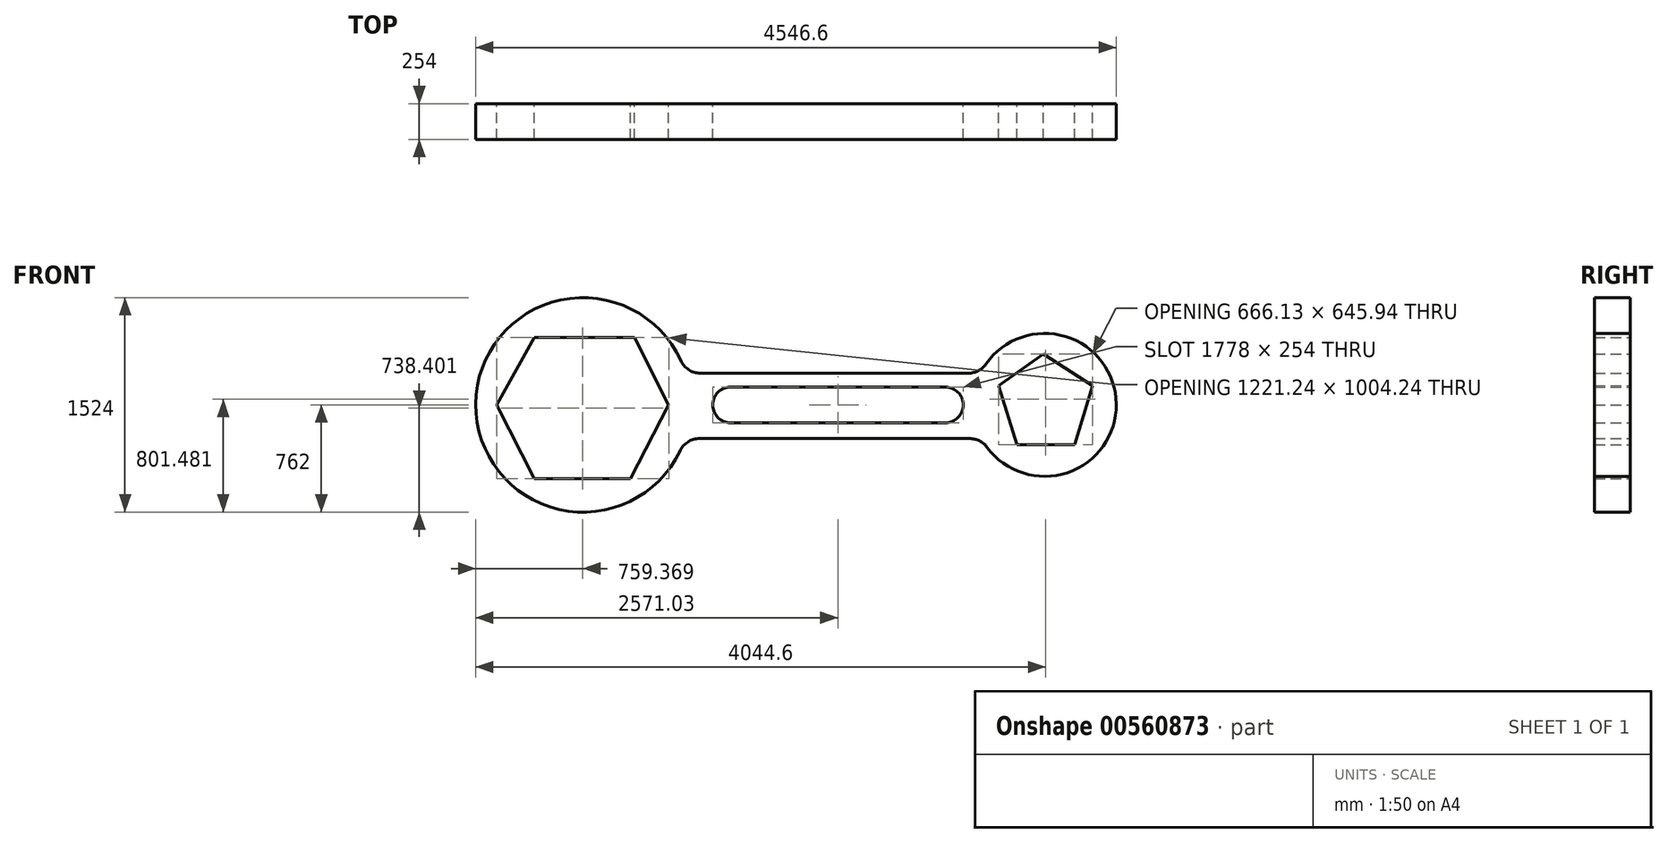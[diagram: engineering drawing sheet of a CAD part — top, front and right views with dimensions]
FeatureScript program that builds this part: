
annotation { "Feature Type Name" : "Feature", "Feature Type Description" : "" }
export const myFeature = defineFeature(function(context is Context, id is Id, definition is map)
    precondition{}
    {
        {
            var Q0;
            Q0=qCreatedBy(makeId("Front.planeOp"),FACE);
            var sketch = newSketch(context, id + "F0", { "sketchPlane" : qUnion([Q0])});
            skCircle(sketch, "E0", {"center": v(0, 0) * mm, "radius": 762 * mm});
            skCircle(sketch, "E1", {"center": v(3276.6, 0) * mm, "radius": 508 * mm});
            skLineSegment(sketch, "E2", {"start": v(826.19, -239.44) * mm, "end": v(2745, -239.44) * mm});
            skLineSegment(sketch, "E3", {"start": v(832.8, 225.17) * mm, "end": v(2734.78, 225.17) * mm});
            skArc(sketch, "E4", {"start": v(694, 314.64) * mm, "mid": v(750.24, 249.47) * mm, "end": v(832.8, 225.17) * mm});
            skArc(sketch, "E5", {"start": v(826.19, -239.44) * mm, "mid": v(744.72, -263.04) * mm, "end": v(688.5, -326.53) * mm});
            skArc(sketch, "E6", {"start": v(2867.68, -301.42) * mm, "mid": v(2813.73, -255.82) * mm, "end": v(2745, -239.44) * mm});
            skArc(sketch, "E7", {"start": v(2734.78, 225.17) * mm, "mid": v(2805.3, 242.46) * mm, "end": v(2859.81, 290.44) * mm});
            skLineSegment(sketch, "E8", {"start": v(1047.03, 127) * mm, "end": v(2576.07, 127) * mm});
            skLineSegment(sketch, "E9", {"start": v(1047.03, -127) * mm, "end": v(2576.07, -127) * mm});
            skArc(sketch, "E10", {"start": v(2571.03, -127) * mm, "mid": v(2698.03, 0) * mm, "end": v(2571.03, 127) * mm});
            skArc(sketch, "E11", {"start": v(1047.03, 127) * mm, "mid": v(920.03, 0) * mm, "end": v(1047.03, -127) * mm});
            skLineSegment(sketch, "E12", {"start": v(-345.79, 478.52) * mm, "end": v(365.76, 478.52) * mm});
            skLineSegment(sketch, "E13", {"start": v(365.76, 478.52) * mm, "end": v(607.99, 0) * mm});
            skLineSegment(sketch, "E14", {"start": v(607.99, 0) * mm, "end": v(335.48, -525.72) * mm});
            skLineSegment(sketch, "E15", {"start": v(335.48, -525.72) * mm, "end": v(-345.79, -525.72) * mm});
            skLineSegment(sketch, "E16", {"start": v(-345.79, -525.72) * mm, "end": v(-613.25, 0) * mm});
            skLineSegment(sketch, "E17", {"start": v(-613.25, 0) * mm, "end": v(-345.79, 478.52) * mm});
            skLineSegment(sketch, "E18", {"start": v(3267.46, 362.45) * mm, "end": v(2949.53, 135.36) * mm});
            skLineSegment(sketch, "E19", {"start": v(3615.66, 135.36) * mm, "end": v(3267.46, 362.45) * mm});
            skLineSegment(sketch, "E20", {"start": v(2949.53, 135.36) * mm, "end": v(3080.74, -283.5) * mm});
            skLineSegment(sketch, "E21", {"start": v(3080.74, -283.5) * mm, "end": v(3489.5, -283.5) * mm});
            skLineSegment(sketch, "E22", {"start": v(3489.5, -283.5) * mm, "end": v(3615.66, 135.36) * mm});
            skSolve(sketch);
        }
        {
            var Q0;
            Q0=makeQuery(id+"F0.imprint","IMPRINT",FACE,{"disambiguationData":[TD([[makeQuery(id+"F0.imprint","IMPRINT",EDGE,{"derivedFrom":sQuery(id+"F0.wireOp",EDGE,"E18")}),-1.0]])]});
            var Q1;
            Q1=makeQuery(id+"F0.imprint","IMPRINT",FACE,{"disambiguationData":[TD([[makeQuery(id+"F0.imprint","IMPRINT",EDGE,{"derivedFrom":sQuery(id+"F0.wireOp",EDGE,"E2")}),1.0]])]});
            var Q2;
            Q2=makeQuery(id+"F0.imprint","IMPRINT",FACE,{"disambiguationData":[TD([[makeQuery(id+"F0.imprint","IMPRINT",EDGE,{"derivedFrom":sQuery(id+"F0.wireOp",EDGE,"E12")}),1.0]])]});
            extrude(context, id + "F1", {"entities" : qUnion([Q0, Q1, Q2]), "depth" : 254 * mm, "offsetDistance" : 25.4 * mm});
        }
    });
